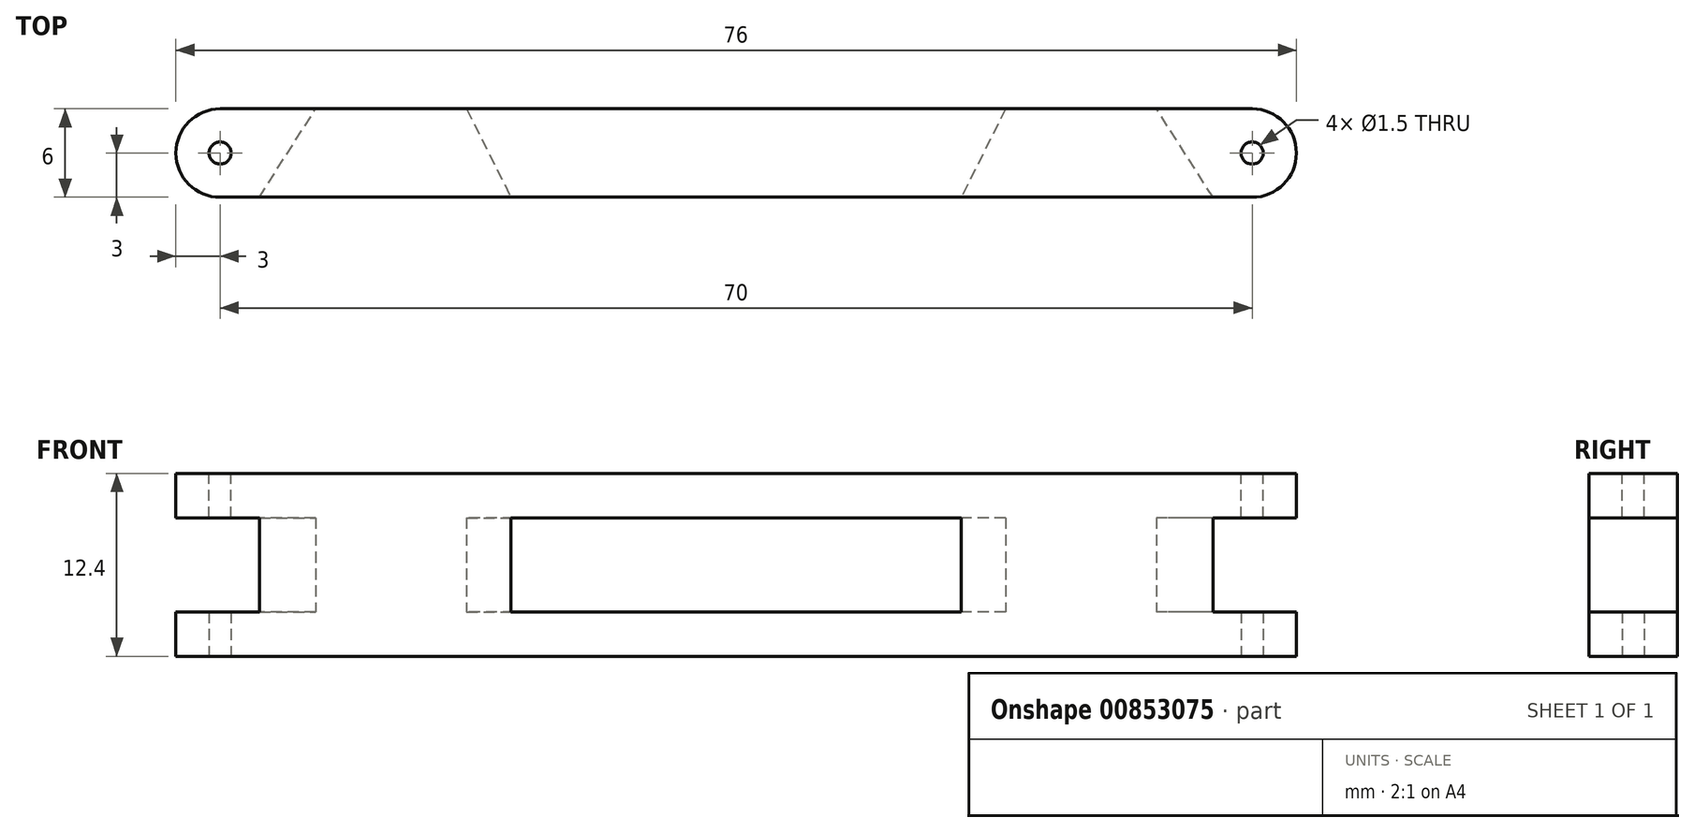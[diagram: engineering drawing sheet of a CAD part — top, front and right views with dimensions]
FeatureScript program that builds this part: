
annotation { "Feature Type Name" : "Feature", "Feature Type Description" : "" }
export const myFeature = defineFeature(function(context is Context, id is Id, definition is map)
    precondition{}
    {
        {
            var Q0;
            Q0=qCreatedBy(makeId("Top.planeOp"),FACE);
            var sketch = newSketch(context, id + "F0", { "sketchPlane" : qUnion([Q0])});
            skLineSegment(sketch, "E0.bottom", {"start": v(35, 3) * mm, "end": v(-35, 3) * mm});
            skLineSegment(sketch, "E0.top", {"start": v(35, -3) * mm, "end": v(-35, -3) * mm});
            skPoint(sketch, "E0.middle", {"position": v(0, 0) * mm});
            skArc(sketch, "E1", {"start": v(-35, 3) * mm, "mid": v(-38, 0) * mm, "end": v(-35, -3) * mm});
            skArc(sketch, "E2.MirrorCS", {"start": v(35, 3) * mm, "mid": v(38, 0) * mm, "end": v(35, -3) * mm});
            skCircle(sketch, "E3", {"center": v(-35, 0) * mm, "radius": 0.75 * mm});
            skCircle(sketch, "E4", {"center": v(35, 0) * mm, "radius": 0.75 * mm});
            skSolve(sketch);
        }
        {
            var Q0;
            Q0 = qSketchRegion(id + "F0", true);
            extrude(context, id + "F1", {"entities" : qUnion([Q0]), "depth" : 3 * mm, "offsetDistance" : 25 * mm});
        }
        {
            var Q0;
            Q0=makeQuery(id+"F1.opExtrude","CAP_FACE",FACE,{"disambiguationData":[OSD([sQuery(id+"F0.wireOp",EDGE,"E0.bottom"),sQuery(id+"F0.wireOp",EDGE,"E0.top"),sQuery(id+"F0.wireOp",EDGE,"E1"),sQuery(id+"F0.wireOp",EDGE,"E2.MirrorCS"),sQuery(id+"F0.wireOp",EDGE,"E3"),sQuery(id+"F0.wireOp",EDGE,"E4")])],"isStart":false});
            var sketch = newSketch(context, id + "F2", { "sketchPlane" : qUnion([Q0])});
            skLineSegment(sketch, "E5", {"start": v(-32.34, -3) * mm, "end": v(-28.52, 3) * mm});
            skLineSegment(sketch, "E6", {"start": v(-35, 0) * mm, "end": v(-12.54, 0) * mm, "construction": true});
            skLineSegment(sketch, "E7", {"start": v(-18.28, 3) * mm, "end": v(-15.27, -3) * mm});
            skLineSegment(sketch, "E8", {"start": v(-15.27, -3) * mm, "end": v(-32.34, -3) * mm});
            skLineSegment(sketch, "E9", {"start": v(-28.52, 3) * mm, "end": v(-18.28, 3) * mm});
            skLineSegment(sketch, "E10.MirrorCS", {"start": v(15.27, -3) * mm, "end": v(32.34, -3) * mm});
            skLineSegment(sketch, "E11.MirrorCS", {"start": v(28.52, 3) * mm, "end": v(18.28, 3) * mm});
            skLineSegment(sketch, "E12.MirrorCS", {"start": v(32.34, -3) * mm, "end": v(28.52, 3) * mm});
            skLineSegment(sketch, "E13.MirrorCS", {"start": v(18.28, 3) * mm, "end": v(15.27, -3) * mm});
            skSolve(sketch);
        }
        {
            var Q0;
            Q0 = qSketchRegion(id + "F2", true);
            extrude(context, id + "F3", {"entities" : qUnion([Q0]), "operationType" : NewBodyOperationType.ADD, "depth" : 3.2 * mm, "offsetDistance" : 25 * mm});
        }
        {
            var Q0;
            Q0=makeQuery(id+"F1.opExtrude","SWEPT_BODY",BODY,{"disambiguationData":[OSD([sQuery(id+"F0.wireOp",EDGE,"E0.bottom"),sQuery(id+"F0.wireOp",EDGE,"E0.top"),sQuery(id+"F0.wireOp",EDGE,"E1"),sQuery(id+"F0.wireOp",EDGE,"E2.MirrorCS"),sQuery(id+"F0.wireOp",EDGE,"E3"),sQuery(id+"F0.wireOp",EDGE,"E4")])]});
            var Q1;
            Q1=makeQuery(id+"F3.opExtrude","CAP_FACE",FACE,{"disambiguationData":[OSD([sQuery(id+"F2.wireOp",EDGE,"E10.MirrorCS"),sQuery(id+"F2.wireOp",EDGE,"E11.MirrorCS"),sQuery(id+"F2.wireOp",EDGE,"E12.MirrorCS"),sQuery(id+"F2.wireOp",EDGE,"E13.MirrorCS")])],"isStart":false});
            mirror(context, id + "F4", {"operationType" : NewBodyOperationType.ADD, "entities" : qUnion([Q0]), "mirrorPlane" : qUnion([Q1])});
        }
    });
